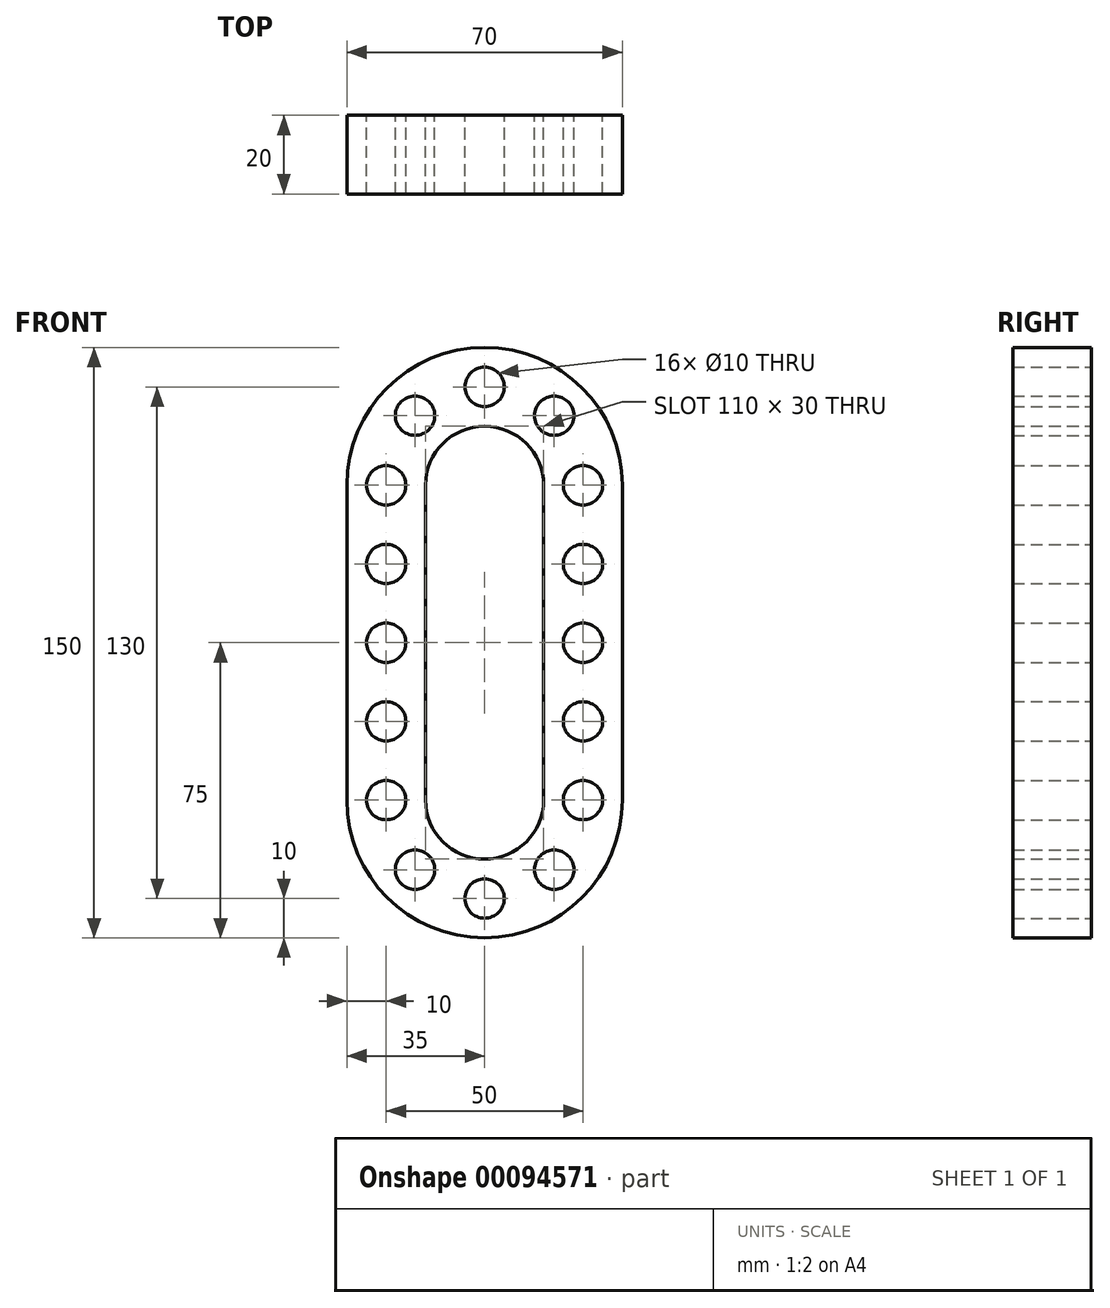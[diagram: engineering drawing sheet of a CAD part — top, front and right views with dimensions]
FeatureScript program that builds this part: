
annotation { "Feature Type Name" : "Feature", "Feature Type Description" : "" }
export const myFeature = defineFeature(function(context is Context, id is Id, definition is map)
    precondition{}
    {
        {
            var Q0;
            Q0=qCreatedBy(makeId("Front.planeOp"),FACE);
            var sketch = newSketch(context, id + "F0", { "sketchPlane" : qUnion([Q0])});
            skPoint(sketch, "E0", {"position": v(-25, 40) * mm});
            skLineSegment(sketch, "E1", {"start": v(-25, 40) * mm, "end": v(-25, 0) * mm, "construction": true});
            skArc(sketch, "E2", {"start": v(0, 65) * mm, "mid": v(-17.68, 57.68) * mm, "end": v(-25, 40) * mm, "construction": true});
            skArc(sketch, "E3.0.startCap", {"start": v(0, 75) * mm, "mid": v(10, 65) * mm, "end": v(0, 55) * mm, "construction": true});
            skArc(sketch, "E3.0.endCap", {"start": v(-15, 40) * mm, "mid": v(-25, 30) * mm, "end": v(-35, 40) * mm, "construction": true});
            skArc(sketch, "E3.0.left", {"start": v(0, 55) * mm, "mid": v(-10.6, 50.6) * mm, "end": v(-15, 40) * mm});
            skArc(sketch, "E3.0.right", {"start": v(0, 75) * mm, "mid": v(-24.75, 64.75) * mm, "end": v(-35, 40) * mm});
            skArc(sketch, "E3.1.startCap", {"start": v(-35, 40) * mm, "mid": v(-25, 50) * mm, "end": v(-15, 40) * mm, "construction": true});
            skArc(sketch, "E3.1.endCap", {"start": v(-15, 0) * mm, "mid": v(-25, -10) * mm, "end": v(-35, 0) * mm, "construction": true});
            skLineSegment(sketch, "E3.1.left", {"start": v(-15, 40) * mm, "end": v(-15, 0) * mm});
            skLineSegment(sketch, "E3.1.right", {"start": v(-35, 40) * mm, "end": v(-35, 0) * mm});
            skCircle(sketch, "E4", {"center": v(-25, 40) * mm, "radius": 5 * mm});
            skPoint(sketch, "E5.center", {"position": v(0, 0) * mm});
            skCircle(sketch, "E6.1.0", {"center": v(-17.68, 57.68) * mm, "radius": 5 * mm});
            skCircle(sketch, "E6.2.0", {"center": v(0, 65) * mm, "radius": 5 * mm});
            skLineSegment(sketch, "E6.anchor1", {"start": v(0, 40) * mm, "end": v(-25, 40) * mm, "construction": true});
            skLineSegment(sketch, "E6.anchor2", {"start": v(0, 40) * mm, "end": v(0, 65) * mm, "construction": true});
            skCircle(sketch, "E7.0.1.0", {"center": v(-25, 20) * mm, "radius": 5 * mm});
            skCircle(sketch, "E7.0.2.0", {"center": v(-25, 0) * mm, "radius": 5 * mm});
            skLineSegment(sketch, "E7.direction1", {"start": v(-25, 40) * mm, "end": v(0, 40) * mm, "construction": true});
            skLineSegment(sketch, "E7.direction2", {"start": v(-25, 40) * mm, "end": v(-25, 20) * mm, "construction": true});
            skLineSegment(sketch, "E8", {"start": v(0, 75) * mm, "end": v(0, 55) * mm});
            skLineSegment(sketch, "E9", {"start": v(-35, 0) * mm, "end": v(-15, 0) * mm});
            skSolve(sketch);
        }
        {
            var Q0;
            {var subQ5=sQuery(id+"F0.wireOp",EDGE,"E3.0.left");Q0=makeQuery(id+"F0.imprint","IMPRINT",FACE,{"disambiguationData":[TD([[makeQuery(id+"F0.imprint","IMPRINT",EDGE,{"derivedFrom":subQ5}),-1.0]])]});}
            extrude(context, id + "F1", {"entities" : qUnion([Q0]), "depth" : 20 * mm});
        }
        {
            var Q0;
            Q0=makeQuery(id+"F1.opExtrude","SWEPT_BODY",BODY,{"disambiguationData":[OSD([sQuery(id+"F0.wireOp",EDGE,"E3.0.left"),sQuery(id+"F0.wireOp",EDGE,"E3.0.right"),sQuery(id+"F0.wireOp",EDGE,"E3.1.left"),sQuery(id+"F0.wireOp",EDGE,"E3.1.right"),sQuery(id+"F0.wireOp",EDGE,"E4"),sQuery(id+"F0.wireOp",EDGE,"E6.1.0"),sQuery(id+"F0.wireOp",EDGE,"E6.2.0"),sQuery(id+"F0.wireOp",EDGE,"E7.0.1.0"),sQuery(id+"F0.wireOp",EDGE,"E7.0.2.0"),sQuery(id+"F0.wireOp",EDGE,"E8"),sQuery(id+"F0.wireOp",EDGE,"E9")])]});
            var Q1;
            Q1=qCreatedBy(makeId("Top.planeOp"),FACE);
            mirror(context, id + "F2", {"operationType" : NewBodyOperationType.ADD, "entities" : qUnion([Q0]), "mirrorPlane" : qUnion([Q1])});
        }
        {
            var Q0;
            Q0=makeQuery(id+"F1.opExtrude","SWEPT_BODY",BODY,{"disambiguationData":[OSD([sQuery(id+"F0.wireOp",EDGE,"E3.0.left"),sQuery(id+"F0.wireOp",EDGE,"E3.0.right"),sQuery(id+"F0.wireOp",EDGE,"E3.1.left"),sQuery(id+"F0.wireOp",EDGE,"E3.1.right"),sQuery(id+"F0.wireOp",EDGE,"E4"),sQuery(id+"F0.wireOp",EDGE,"E6.1.0"),sQuery(id+"F0.wireOp",EDGE,"E6.2.0"),sQuery(id+"F0.wireOp",EDGE,"E7.0.1.0"),sQuery(id+"F0.wireOp",EDGE,"E7.0.2.0"),sQuery(id+"F0.wireOp",EDGE,"E8"),sQuery(id+"F0.wireOp",EDGE,"E9")])]});
            var Q1;
            Q1=qCreatedBy(makeId("Right.planeOp"),FACE);
            mirror(context, id + "F3", {"operationType" : NewBodyOperationType.ADD, "entities" : qUnion([Q0]), "mirrorPlane" : qUnion([Q1])});
        }
    });
